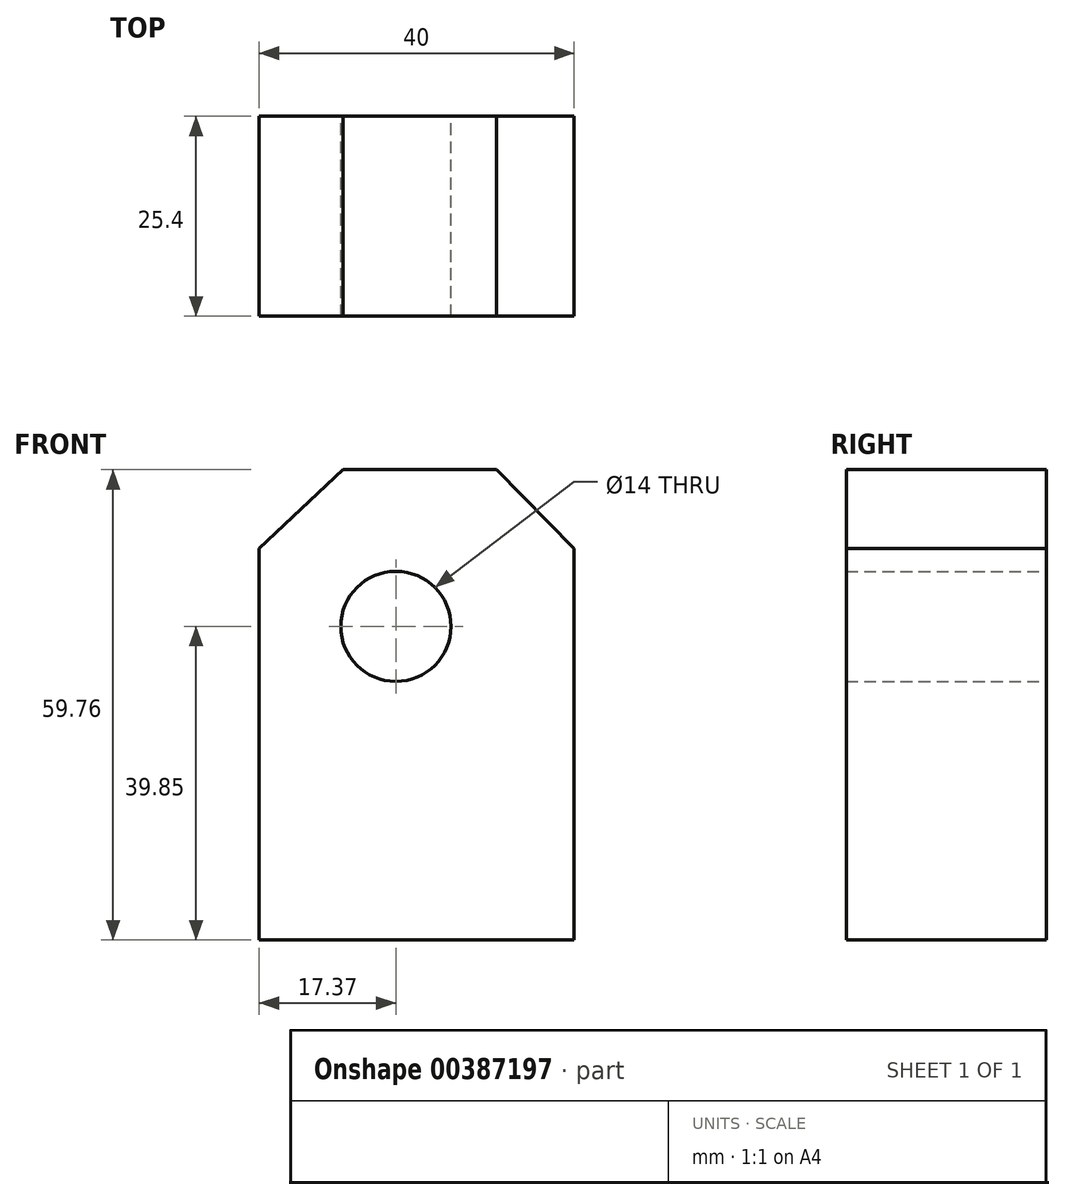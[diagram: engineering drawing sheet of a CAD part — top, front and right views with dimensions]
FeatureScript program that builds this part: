
annotation { "Feature Type Name" : "Feature", "Feature Type Description" : "" }
export const myFeature = defineFeature(function(context is Context, id is Id, definition is map)
    precondition{}
    {
        {
            var Q0;
            Q0=qCreatedBy(makeId("Front.planeOp"),FACE);
            var sketch = newSketch(context, id + "F0", { "sketchPlane" : qUnion([Q0])});
            skCircle(sketch, "E0", {"center": v(0, 0) * mm, "radius": 7 * mm});
            skLineSegment(sketch, "E1", {"start": v(-17.37, 9.9) * mm, "end": v(-17.37, -39.85) * mm});
            skLineSegment(sketch, "E2", {"start": v(22.63, 9.9) * mm, "end": v(22.63, -37.03) * mm});
            skLineSegment(sketch, "E3", {"start": v(-17.37, -39.85) * mm, "end": v(22.63, -39.85) * mm});
            skLineSegment(sketch, "E4", {"start": v(22.63, -37.03) * mm, "end": v(22.63, -39.85) * mm});
            skPoint(sketch, "E5.end.orphan", {"position": v(8.23, 18.14) * mm});
            skLineSegment(sketch, "E6", {"start": v(22.63, 9.9) * mm, "end": v(12.8, 19.91) * mm});
            skPoint(sketch, "E7.start.orphan", {"position": v(-7.62, 18.14) * mm});
            skLineSegment(sketch, "E8", {"start": v(12.8, 19.91) * mm, "end": v(-6.7, 19.91) * mm});
            skLineSegment(sketch, "E9", {"start": v(-17.37, 9.9) * mm, "end": v(-6.7, 19.91) * mm});
            skSolve(sketch);
        }
        {
            var Q0;
            Q0 = qSketchRegion(id + "F0", true);
            extrude(context, id + "F1", {"entities" : qUnion([Q0]), "depth" : 25.4 * mm});
        }
    });
